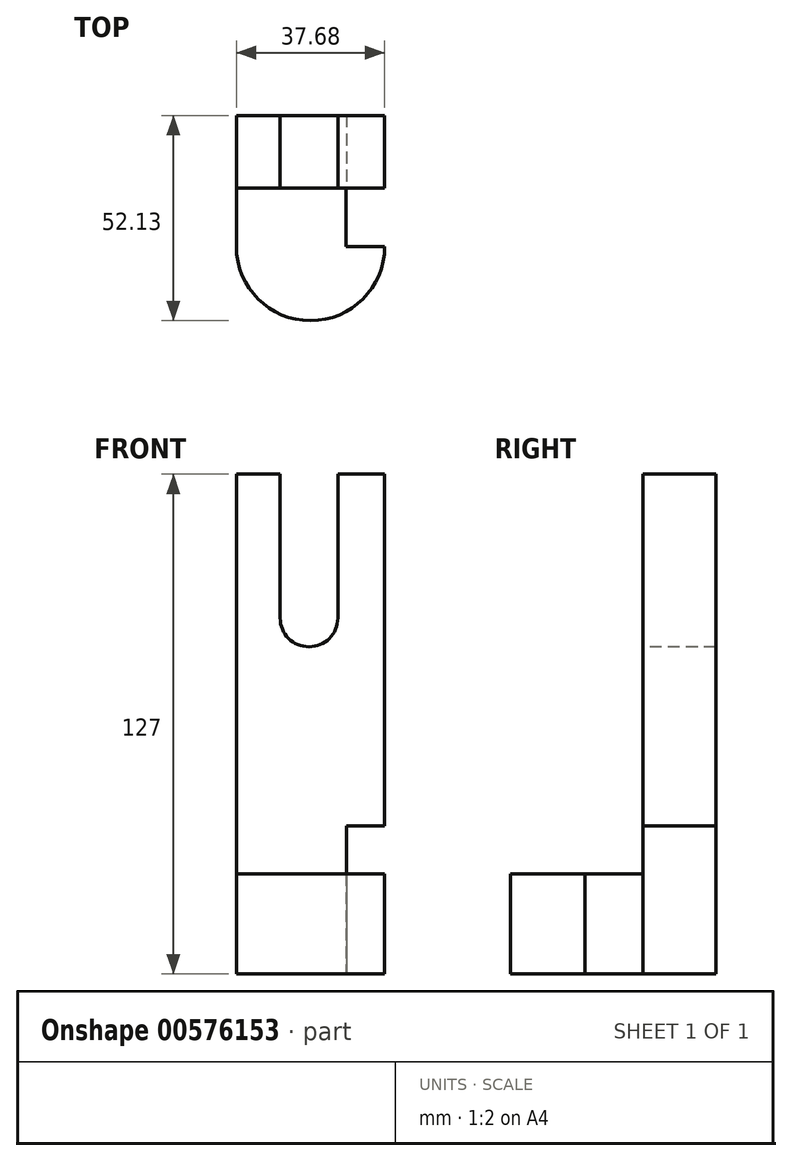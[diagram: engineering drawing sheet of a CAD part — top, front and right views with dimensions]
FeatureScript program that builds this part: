
annotation { "Feature Type Name" : "Feature", "Feature Type Description" : "" }
export const myFeature = defineFeature(function(context is Context, id is Id, definition is map)
    precondition{}
    {
        {
            var Q0;
            Q0=qCreatedBy(makeId("Top.planeOp"),FACE);
            var sketch = newSketch(context, id + "F0", { "sketchPlane" : qUnion([Q0])});
            skArc(sketch, "E0", {"start": v(18.84, 0) * mm, "mid": v(0, -18.84) * mm, "end": v(-18.84, 0) * mm});
            skLineSegment(sketch, "E1", {"start": v(-18.84, 0) * mm, "end": v(18.84, 0) * mm});
            skLineSegment(sketch, "E2", {"start": v(-18.84, 0) * mm, "end": v(-18.84, 33.29) * mm});
            skLineSegment(sketch, "E3", {"start": v(-18.84, 33.29) * mm, "end": v(18.84, 33.29) * mm});
            skLineSegment(sketch, "E4", {"start": v(18.84, 33.29) * mm, "end": v(18.84, 14.83) * mm});
            skLineSegment(sketch, "E5", {"start": v(18.84, 14.83) * mm, "end": v(8.95, 14.83) * mm});
            skLineSegment(sketch, "E6", {"start": v(8.95, 14.83) * mm, "end": v(8.95, 0) * mm});
            skSolve(sketch);
        }
        {
            var Q0;
            Q0 = qSketchRegion(id + "F0", true);
            extrude(context, id + "F1", {"entities" : qUnion([Q0]), "depth" : 25.4 * mm, "offsetDistance" : 25.4 * mm});
        }
        {
            var Q0;
            Q0=makeQuery(id+"F1.opExtrude","CAP_FACE",FACE,{"disambiguationData":[OSD([sQuery(id+"F0.wireOp",EDGE,"E0"),sQuery(id+"F0.wireOp",EDGE,"E1"),sQuery(id+"F0.wireOp",EDGE,"E2"),sQuery(id+"F0.wireOp",EDGE,"E3"),sQuery(id+"F0.wireOp",EDGE,"E4"),sQuery(id+"F0.wireOp",EDGE,"E5"),sQuery(id+"F0.wireOp",EDGE,"E6")])],"isStart":false});
            var sketch = newSketch(context, id + "F2", { "sketchPlane" : qUnion([Q0])});
            skLineSegment(sketch, "E7.bottom", {"start": v(18.84, 14.83) * mm, "end": v(-18.84, 14.83) * mm});
            skLineSegment(sketch, "E7.top", {"start": v(18.84, 33.29) * mm, "end": v(-18.84, 33.29) * mm});
            skLineSegment(sketch, "E7.left", {"start": v(18.84, 14.83) * mm, "end": v(18.84, 33.29) * mm});
            skLineSegment(sketch, "E7.right", {"start": v(-18.84, 14.83) * mm, "end": v(-18.84, 33.29) * mm});
            skSolve(sketch);
        }
        {
            var Q0;
            Q0 = qSketchRegion(id + "F2", true);
            extrude(context, id + "F3", {"entities" : qUnion([Q0]), "operationType" : NewBodyOperationType.ADD, "depth" : 101.6 * mm, "offsetDistance" : 25.4 * mm});
        }
        {
            var Q0;
            Q0=makeQuery(id+"F3.boolean.opBoolean","MERGE",FACE,{"derivedFrom":[makeQuery(id+"F1.opExtrude","SWEPT_FACE",FACE,{"disambiguationData":[OSD([sQuery(id+"F0.wireOp",EDGE,"E5")])]}),makeQuery(id+"F3.opExtrude","SWEPT_FACE",FACE,{"disambiguationData":[OSD([sQuery(id+"F2.wireOp",EDGE,"E7.bottom")])]})]});
            var sketch = newSketch(context, id + "F4", { "sketchPlane" : qUnion([Q0])});
            skLineSegment(sketch, "E8.bottom", {"start": v(-7.71, 127) * mm, "end": v(6.92, 127) * mm});
            skLineSegment(sketch, "E8.top", {"start": v(-7.71, 90.45) * mm, "end": v(6.92, 90.45) * mm});
            skLineSegment(sketch, "E8.left", {"start": v(-7.71, 127) * mm, "end": v(-7.71, 90.45) * mm});
            skLineSegment(sketch, "E8.right", {"start": v(6.92, 127) * mm, "end": v(6.92, 90.45) * mm});
            skArc(sketch, "E9", {"start": v(6.92, 90.45) * mm, "mid": v(-0.4, 83.14) * mm, "end": v(-7.71, 90.45) * mm});
            skSolve(sketch);
        }
        {
            var Q0;
            Q0 = qSketchRegion(id + "F4", true);
            extrude(context, id + "F5", {"entities" : qUnion([Q0]), "operationType" : NewBodyOperationType.REMOVE, "oppositeDirection" : true, "depth" : 25.4 * mm, "offsetDistance" : 25.4 * mm});
        }
        {
            var Q0;
            Q0 = qSketchRegion(id + "F4", true);
            extrude(context, id + "F6", {"entities" : qUnion([Q0]), "operationType" : NewBodyOperationType.REMOVE, "oppositeDirection" : true, "depth" : 25.4 * mm, "offsetDistance" : 25.4 * mm});
        }
        {
            var Q0;
            Q0=makeQuery(id+"F3.boolean.opBoolean","MERGE",FACE,{"derivedFrom":[makeQuery(id+"F1.opExtrude","SWEPT_FACE",FACE,{"disambiguationData":[OSD([sQuery(id+"F0.wireOp",EDGE,"E4")])]}),makeQuery(id+"F3.opExtrude","SWEPT_FACE",FACE,{"disambiguationData":[OSD([sQuery(id+"F2.wireOp",EDGE,"E7.left")])]})]});
            var sketch = newSketch(context, id + "F7", { "sketchPlane" : qUnion([Q0])});
            skLineSegment(sketch, "E10.bottom", {"start": v(14.83, 37.64) * mm, "end": v(33.29, 37.64) * mm});
            skLineSegment(sketch, "E10.top", {"start": v(14.83, 0) * mm, "end": v(33.29, 0) * mm});
            skLineSegment(sketch, "E10.left", {"start": v(14.83, 37.64) * mm, "end": v(14.83, 0) * mm});
            skLineSegment(sketch, "E10.right", {"start": v(33.29, 37.64) * mm, "end": v(33.29, 0) * mm});
            skSolve(sketch);
        }
        {
            var Q0;
            Q0 = qSketchRegion(id + "F7", true);
            extrude(context, id + "F8", {"entities" : qUnion([Q0]), "operationType" : NewBodyOperationType.REMOVE, "oppositeDirection" : true, "depth" : 9.65 * mm, "offsetDistance" : 25.4 * mm});
        }
    });
